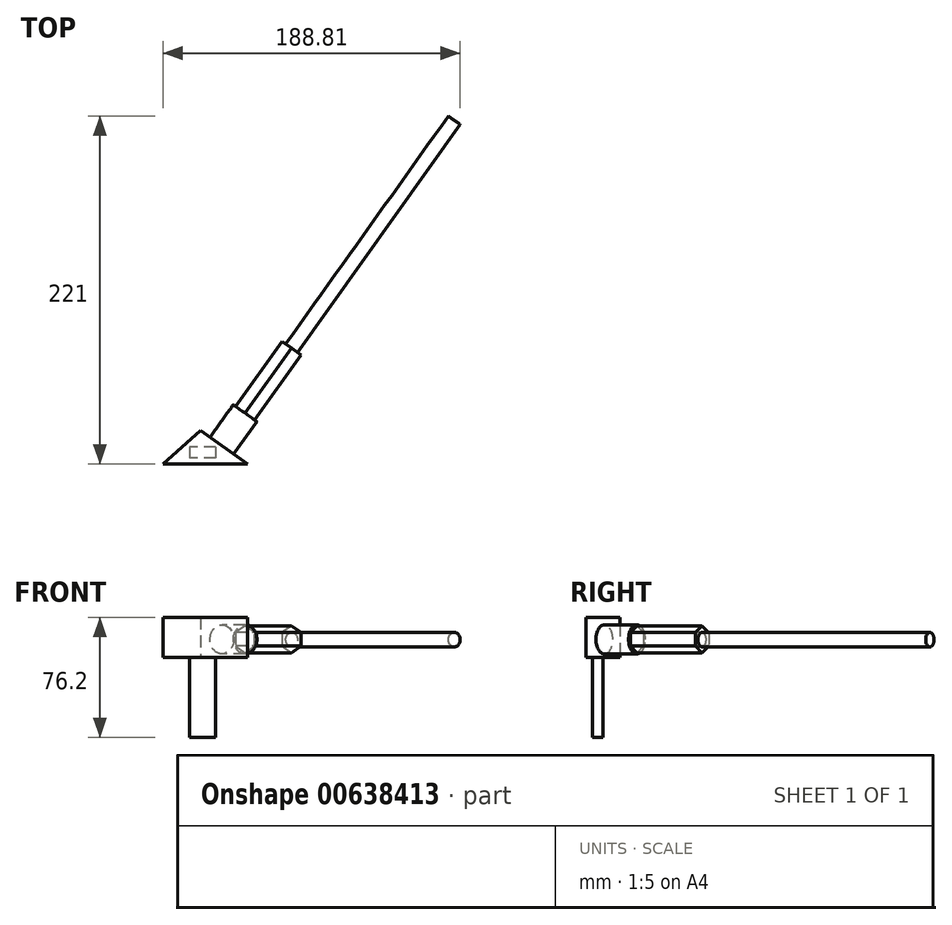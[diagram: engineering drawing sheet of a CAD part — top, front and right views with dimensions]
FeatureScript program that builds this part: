
annotation { "Feature Type Name" : "Feature", "Feature Type Description" : "" }
export const myFeature = defineFeature(function(context is Context, id is Id, definition is map)
    precondition{}
    {
        {
            var Q0;
            Q0=qCreatedBy(makeId("Top.planeOp"),FACE);
            var sketch = newSketch(context, id + "F0", { "sketchPlane" : qUnion([Q0])});
            skLineSegment(sketch, "E0", {"start": v(-53.74, 31.25) * mm, "end": v(0, 31.25) * mm});
            skLineSegment(sketch, "E1", {"start": v(-23.87, 35.3) * mm, "end": v(0, 31.25) * mm});
            skLineSegment(sketch, "E2", {"start": v(-23.87, 35.3) * mm, "end": v(-41.94, 31.25) * mm});
            skLineSegment(sketch, "E3", {"start": v(-41.94, 31.25) * mm, "end": v(-25.53, 42.3) * mm});
            skLineSegment(sketch, "E4", {"start": v(-25.53, 42.3) * mm, "end": v(-23.87, 35.3) * mm});
            skLineSegment(sketch, "E5", {"start": v(-25.53, 42.3) * mm, "end": v(0, 31.25) * mm});
            skLineSegment(sketch, "E6", {"start": v(-53.74, 31.25) * mm, "end": v(-29.96, 52.63) * mm});
            skLineSegment(sketch, "E7", {"start": v(-29.96, 52.63) * mm, "end": v(-25.53, 42.3) * mm});
            skLineSegment(sketch, "E8", {"start": v(-29.96, 52.63) * mm, "end": v(0, 31.25) * mm});
            skSolve(sketch);
        }
        {
            var Q0;
            Q0 = qSketchRegion(id + "F0", true);
            extrude(context, id + "F1", {"entities" : qUnion([Q0]), "depth" : 25.4 * mm, "offsetDistance" : 25.4 * mm});
        }
        {
            var Q0;
            Q0=makeQuery(id+"F1.opExtrude","SWEPT_FACE",FACE,{"disambiguationData":[OSD([sQuery(id+"F0.wireOp",EDGE,"E8")])]});
            var sketch = newSketch(context, id + "F2", { "sketchPlane" : qUnion([Q0])});
            skCircle(sketch, "E9", {"center": v(38.15, 11.52) * mm, "radius": 9.2 * mm});
            skSolve(sketch);
        }
        {
            var Q0;
            Q0 = qSketchRegion(id + "F2", true);
            extrude(context, id + "F3", {"entities" : qUnion([Q0]), "operationType" : NewBodyOperationType.ADD, "depth" : 25.4 * mm, "offsetDistance" : 25.4 * mm});
        }
        {
            var Q0;
            Q0=makeQuery(id+"F1.opExtrude","CAP_FACE",FACE,{"disambiguationData":[OSD([sQuery(id+"F0.wireOp",EDGE,"E0"),sQuery(id+"F0.wireOp",EDGE,"E6"),sQuery(id+"F0.wireOp",EDGE,"E8")])],"isStart":true});
            var sketch = newSketch(context, id + "F4", { "sketchPlane" : qUnion([Q0])});
            skPoint(sketch, "E10.firstSnap0", {"position": v(-14.98, -41.94) * mm});
            skLineSegment(sketch, "E10.bottom", {"start": v(-20.19, -41.94) * mm, "end": v(-36.78, -41.94) * mm});
            skLineSegment(sketch, "E10.top", {"start": v(-20.19, -35.12) * mm, "end": v(-36.78, -35.12) * mm});
            skLineSegment(sketch, "E10.left", {"start": v(-20.19, -41.94) * mm, "end": v(-20.19, -35.12) * mm});
            skLineSegment(sketch, "E10.right", {"start": v(-36.78, -41.94) * mm, "end": v(-36.78, -35.12) * mm});
            skSolve(sketch);
        }
        {
            var Q0;
            Q0 = qSketchRegion(id + "F4", true);
            extrude(context, id + "F5", {"entities" : qUnion([Q0]), "operationType" : NewBodyOperationType.ADD, "depth" : 25.4 * mm, "offsetDistance" : 25.4 * mm});
        }
        {
            var Q0;
            Q0=makeQuery(id+"F5.opExtrude","CAP_FACE",FACE,{"disambiguationData":[OSD([sQuery(id+"F4.wireOp",EDGE,"E10.bottom"),sQuery(id+"F4.wireOp",EDGE,"E10.top"),sQuery(id+"F4.wireOp",EDGE,"E10.left"),sQuery(id+"F4.wireOp",EDGE,"E10.right")])],"isStart":false});
            extrude(context, id + "F6", {"entities" : qUnion([Q0]), "operationType" : NewBodyOperationType.ADD, "depth" : 25.4 * mm, "offsetDistance" : 25.4 * mm});
        }
        {
            var Q0;
            Q0=makeQuery(id+"F3.opExtrude","CAP_FACE",FACE,{"disambiguationData":[OSD([sQuery(id+"F2.wireOp",EDGE,"E9")])],"isStart":false});
            var sketch = newSketch(context, id + "F7", { "sketchPlane" : qUnion([Q0])});
            skCircle(sketch, "E11.cCircle", {"center": v(38.15, 11.52) * mm, "radius": 7.36 * mm, "construction": true});
            skLineSegment(sketch, "E11.0", {"start": v(45.5, 15.77) * mm, "end": v(45.5, 7.27) * mm});
            skLineSegment(sketch, "E11.1", {"start": v(45.5, 7.27) * mm, "end": v(38.15, 3.03) * mm});
            skLineSegment(sketch, "E11.2", {"start": v(38.15, 3.03) * mm, "end": v(30.79, 7.27) * mm});
            skLineSegment(sketch, "E11.3", {"start": v(30.79, 7.27) * mm, "end": v(30.79, 15.77) * mm});
            skLineSegment(sketch, "E11.4", {"start": v(30.79, 15.77) * mm, "end": v(38.15, 20.02) * mm});
            skLineSegment(sketch, "E11.5", {"start": v(38.15, 20.02) * mm, "end": v(45.5, 15.77) * mm});
            skPoint(sketch, "E11.0.midPoint", {"position": v(45.5, 11.52) * mm});
            skSolve(sketch);
        }
        {
            var Q0;
            Q0 = qSketchRegion(id + "F7", true);
            extrude(context, id + "F8", {"entities" : qUnion([Q0]), "operationType" : NewBodyOperationType.ADD, "depth" : 25.4 * mm, "offsetDistance" : 25.4 * mm});
        }
        {
            var Q0;
            Q0=makeQuery(id+"F8.opExtrude","CAP_FACE",FACE,{"disambiguationData":[OSD([sQuery(id+"F7.wireOp",EDGE,"E11.0"),sQuery(id+"F7.wireOp",EDGE,"E11.1"),sQuery(id+"F7.wireOp",EDGE,"E11.2"),sQuery(id+"F7.wireOp",EDGE,"E11.3"),sQuery(id+"F7.wireOp",EDGE,"E11.4"),sQuery(id+"F7.wireOp",EDGE,"E11.5")])],"isStart":false});
            extrude(context, id + "F9", {"entities" : qUnion([Q0]), "operationType" : NewBodyOperationType.ADD, "depth" : 25.4 * mm, "offsetDistance" : 25.4 * mm});
        }
        {
            var Q0;
            Q0=makeQuery(id+"F9.opExtrude","CAP_FACE",FACE,{"disambiguationData":[OSD([sQuery(id+"F7.wireOp",EDGE,"E11.0"),sQuery(id+"F7.wireOp",EDGE,"E11.1"),sQuery(id+"F7.wireOp",EDGE,"E11.2"),sQuery(id+"F7.wireOp",EDGE,"E11.3"),sQuery(id+"F7.wireOp",EDGE,"E11.4"),sQuery(id+"F7.wireOp",EDGE,"E11.5")])],"isStart":false});
            var sketch = newSketch(context, id + "F10", { "sketchPlane" : qUnion([Q0])});
            skCircle(sketch, "E12", {"center": v(38.11, 11.34) * mm, "radius": 4.6 * mm});
            skSolve(sketch);
        }
        {
            var Q0;
            Q0 = qSketchRegion(id + "F10", true);
            extrude(context, id + "F11", {"entities" : qUnion([Q0]), "operationType" : NewBodyOperationType.ADD, "depth" : 177.8 * mm, "offsetDistance" : 25.4 * mm});
        }
    });
